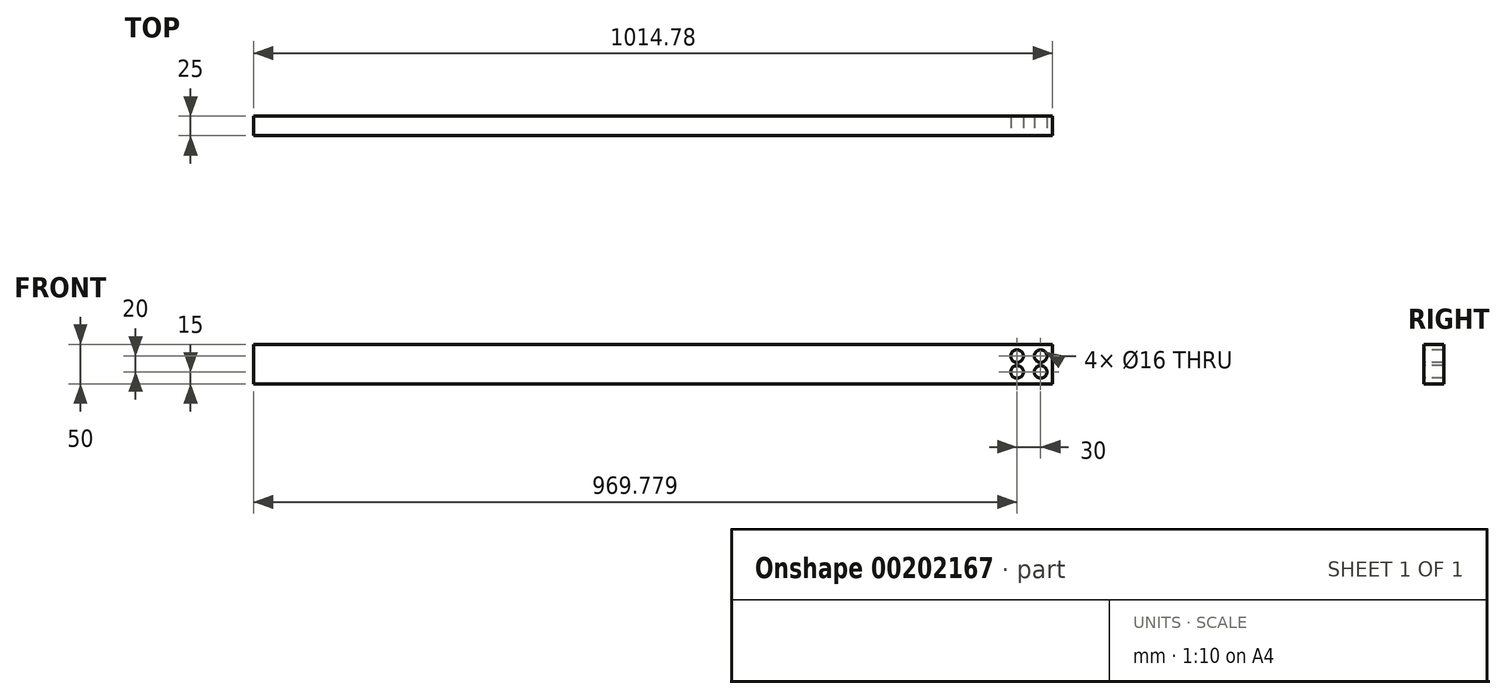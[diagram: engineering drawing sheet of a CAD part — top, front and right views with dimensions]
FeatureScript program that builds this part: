
annotation { "Feature Type Name" : "Feature", "Feature Type Description" : "" }
export const myFeature = defineFeature(function(context is Context, id is Id, definition is map)
    precondition{}
    {
        {
            var Q0;
            Q0=qCreatedBy(makeId("Front.planeOp"),FACE);
            var sketch = newSketch(context, id + "F0", { "sketchPlane" : qUnion([Q0])});
            skLineSegment(sketch, "E0.bottom", {"start": v(507.39, 25) * mm, "end": v(-507.39, 25) * mm});
            skLineSegment(sketch, "E0.top", {"start": v(507.39, -25) * mm, "end": v(-507.39, -25) * mm});
            skLineSegment(sketch, "E0.left", {"start": v(507.39, 25) * mm, "end": v(507.39, -25) * mm});
            skLineSegment(sketch, "E0.right", {"start": v(-507.39, 25) * mm, "end": v(-507.39, -25) * mm});
            skPoint(sketch, "E0.middle", {"position": v(0, 0) * mm});
            skSolve(sketch);
        }
        {
            var Q0;
            Q0=qSketchRegion(id+"F0",true);
            extrude(context, id + "F1", {"entities" : qUnion([Q0]), "depth" : 25 * mm});
        }
        {
            var Q0;
            Q0=makeQuery(id+"F1.opExtrude","CAP_FACE",FACE,{"disambiguationData":[OSD([sQuery(id+"F0.wireOp",EDGE,"E0.bottom"),sQuery(id+"F0.wireOp",EDGE,"E0.top"),sQuery(id+"F0.wireOp",EDGE,"E0.left"),sQuery(id+"F0.wireOp",EDGE,"E0.right")])],"isStart":false});
            var sketch = newSketch(context, id + "F2", { "sketchPlane" : qUnion([Q0])});
            skPoint(sketch, "E1", {"position": v(492.39, 10) * mm});
            skPoint(sketch, "E2", {"position": v(492.39, -10) * mm});
            skPoint(sketch, "E3", {"position": v(462.39, -10) * mm});
            skPoint(sketch, "E4", {"position": v(462.39, 10) * mm});
            skCircle(sketch, "E5", {"center": v(462.39, 10) * mm, "radius": 8 * mm});
            skCircle(sketch, "E6", {"center": v(462.39, -10) * mm, "radius": 8 * mm});
            skCircle(sketch, "E7", {"center": v(492.39, 10) * mm, "radius": 8 * mm});
            skCircle(sketch, "E8", {"center": v(492.39, -10) * mm, "radius": 8 * mm});
            skSolve(sketch);
        }
        {
            var Q0;
            Q0=qSketchRegion(id+"F2",true);
            extrude(context, id + "F3", {"entities" : qUnion([Q0]), "operationType" : NewBodyOperationType.REMOVE, "oppositeDirection" : true, "depth" : 25 * mm});
        }
    });
